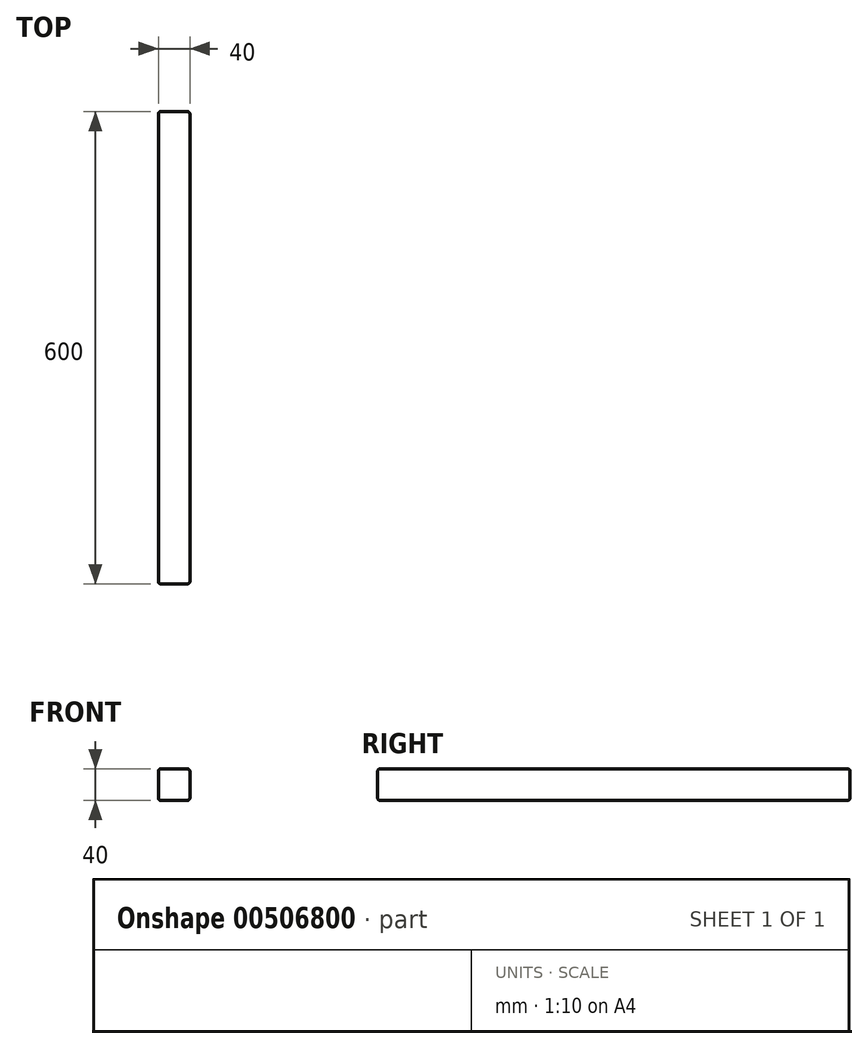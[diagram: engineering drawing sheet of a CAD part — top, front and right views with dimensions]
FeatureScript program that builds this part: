
annotation { "Feature Type Name" : "Feature", "Feature Type Description" : "" }
export const myFeature = defineFeature(function(context is Context, id is Id, definition is map)
    precondition{}
    {
        {
            var Q0;
            Q0=qCreatedBy(makeId("Front.planeOp"),FACE);
            var sketch = newSketch(context, id + "F0", { "sketchPlane" : qUnion([Q0])});
            skLineSegment(sketch, "E0.bottom", {"start": v(-132, 40) * mm, "end": v(-92, 40) * mm});
            skLineSegment(sketch, "E0.top", {"start": v(-132, 0) * mm, "end": v(-92, 0) * mm});
            skLineSegment(sketch, "E0.left", {"start": v(-132, 40) * mm, "end": v(-132, 0) * mm});
            skLineSegment(sketch, "E0.right", {"start": v(-92, 40) * mm, "end": v(-92, 0) * mm});
            skSolve(sketch);
        }
        {
            var Q0;
            Q0 = qSketchRegion(id + "F0", true);
            extrude(context, id + "F1", {"entities" : qUnion([Q0]), "depth" : 600 * mm});
        }
        {
            var Q0;
            Q0=makeQuery(id+"F1.opExtrude","SWEPT_FACE",FACE,{"disambiguationData":[OSD([sQuery(id+"F0.wireOp",EDGE,"E0.bottom")])]});
            var Q1;
            Q1=makeQuery(id+"F1.opExtrude","SWEPT_FACE",FACE,{"disambiguationData":[OSD([sQuery(id+"F0.wireOp",EDGE,"E0.right")])]});
            var Q2;
            Q2=makeQuery(id+"F1.opExtrude","SWEPT_FACE",FACE,{"disambiguationData":[OSD([sQuery(id+"F0.wireOp",EDGE,"E0.top")])]});
            var Q3;
            Q3=makeQuery(id+"F1.opExtrude","SWEPT_FACE",FACE,{"disambiguationData":[OSD([sQuery(id+"F0.wireOp",EDGE,"E0.left")])]});
            fillet(context, id + "F2", {"entities" : qUnion([Q0, Q1, Q2, Q3]), "radius" : 3 * mm, "tangentPropagation" : true, "allowEdgeOverflow" : false});
        }
        {
            var Q0;
            Q0=makeQuery(id+"F1.opExtrude","SWEPT_FACE",FACE,{"disambiguationData":[OSD([sQuery(id+"F0.wireOp",EDGE,"E0.right")])]});
            var sketch = newSketch(context, id + "F3", { "sketchPlane" : qUnion([Q0])});
            skLineSegment(sketch, "E1", {"start": v(-600.36, 20) * mm, "end": v(-585.36, 20) * mm});
            skPoint(sketch, "E1.startSnap0", {"position": v(-597, 20) * mm});
            skLineSegment(sketch, "E2", {"start": v(-585.36, 20) * mm, "end": v(-491.43, 20) * mm});
            skLineSegment(sketch, "E3", {"start": v(-491.43, 20) * mm, "end": v(-117.86, 20) * mm});
            skLineSegment(sketch, "E4", {"start": v(-117.86, 20) * mm, "end": v(-15, 20) * mm});
            skLineSegment(sketch, "E5", {"start": v(-15, 20) * mm, "end": v(0, 20) * mm});
            skSolve(sketch);
        }
        {
            var Q0;
            Q0=makeQuery(id+"F1.opExtrude","SWEPT_FACE",FACE,{"disambiguationData":[OSD([sQuery(id+"F0.wireOp",EDGE,"E0.bottom")])]});
            var sketch = newSketch(context, id + "F4", { "sketchPlane" : qUnion([Q0])});
            skLineSegment(sketch, "E6", {"start": v(-112, -3) * mm, "end": v(-112, -300) * mm});
            skLineSegment(sketch, "E7", {"start": v(-112, -300) * mm, "end": v(-112, -597) * mm});
            skSolve(sketch);
        }
    });
